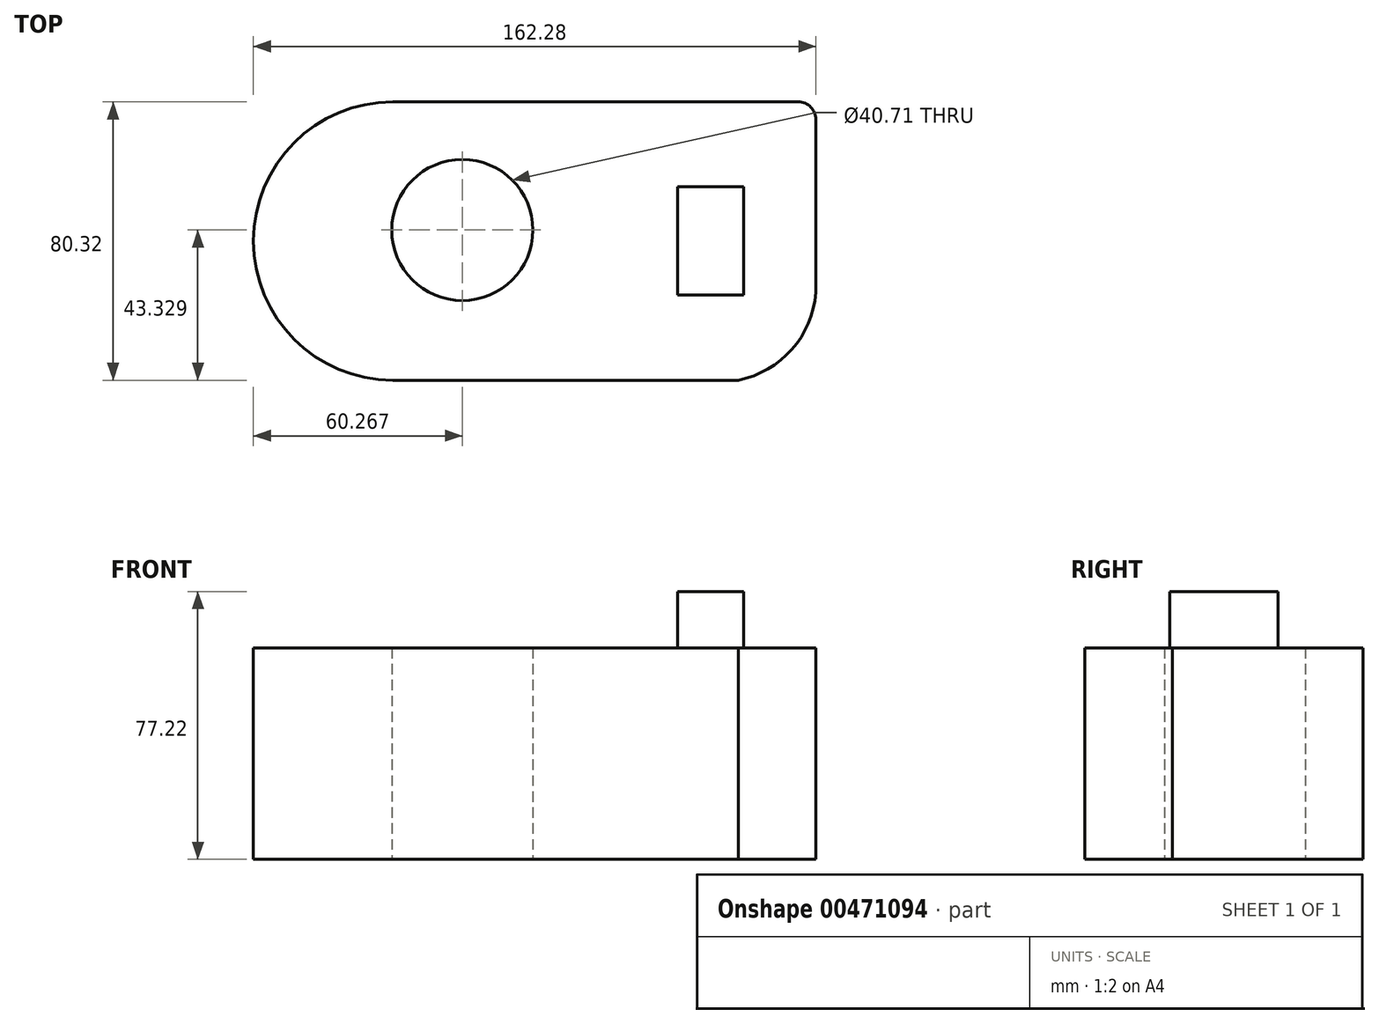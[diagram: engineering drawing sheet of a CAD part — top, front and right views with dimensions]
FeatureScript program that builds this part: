
annotation { "Feature Type Name" : "Feature", "Feature Type Description" : "" }
export const myFeature = defineFeature(function(context is Context, id is Id, definition is map)
    precondition{}
    {
        {
            var Q0;
            Q0=qCreatedBy(makeId("Top.planeOp"),FACE);
            var sketch = newSketch(context, id + "F0", { "sketchPlane" : qUnion([Q0])});
            skLineSegment(sketch, "E0.bottom", {"start": v(61.06, 40.16) * mm, "end": v(-61.06, 40.16) * mm});
            skLineSegment(sketch, "E0.top", {"start": v(38.63, -40.16) * mm, "end": v(-61.06, -40.16) * mm});
            skLineSegment(sketch, "E0.left", {"start": v(61.06, 40.16) * mm, "end": v(61.06, -14.84) * mm});
            skPoint(sketch, "E0.middle", {"position": v(0, 0) * mm});
            skArc(sketch, "E1", {"start": v(-61.06, -40.16) * mm, "mid": v(-101.22, 0) * mm, "end": v(-61.06, 40.16) * mm});
            skArc(sketch, "E2", {"start": v(38.63, -40.16) * mm, "mid": v(54.11, -31.28) * mm, "end": v(61.06, -14.84) * mm});
            skPoint(sketch, "E3.orphan", {"position": v(61.06, -40.16) * mm});
            skCircle(sketch, "E4", {"center": v(-40.95, 3.17) * mm, "radius": 20.35 * mm});
            skPoint(sketch, "E4.second.point", {"position": v(-20.85, 0) * mm});
            skPoint(sketch, "E4.third.point", {"position": v(-61.06, 6.34) * mm});
            skSolve(sketch);
        }
        {
            var Q0;
            Q0=makeQuery(id+"F0.imprint","IMPRINT",FACE,{"disambiguationData":[TD([[makeQuery(id+"F0.imprint","IMPRINT",EDGE,{"derivedFrom":sQuery(id+"F0.wireOp",EDGE,"E0.bottom")}),1.0]])]});
            extrude(context, id + "F1", {"entities" : qUnion([Q0]), "depth" : 60.96 * mm});
        }
        {
            var Q0;
            Q0=makeQuery(id+"F1.opExtrude","SWEPT_EDGE",EDGE,{"disambiguationData":[OSD([sQuery(id+"F0.wireOp",EDGE,"E0.bottom"),sQuery(id+"F0.wireOp",EDGE,"E0.left")])]});
            fillet(context, id + "F2", {"entities" : qUnion([Q0]), "radius" : 5.08 * mm, "tangentPropagation" : true, "allowEdgeOverflow" : false});
        }
        {
            var Q0;
            Q0=makeQuery(id+"F1.opExtrude","CAP_FACE",FACE,{"disambiguationData":[OSD([sQuery(id+"F0.wireOp",EDGE,"E0.bottom"),sQuery(id+"F0.wireOp",EDGE,"E0.top"),sQuery(id+"F0.wireOp",EDGE,"E0.left"),sQuery(id+"F0.wireOp",EDGE,"E1"),sQuery(id+"F0.wireOp",EDGE,"E2"),sQuery(id+"F0.wireOp",EDGE,"E4")])],"isStart":false});
            var sketch = newSketch(context, id + "F3", { "sketchPlane" : qUnion([Q0])});
            skLineSegment(sketch, "E5.bottom", {"start": v(21.18, -15.62) * mm, "end": v(40.24, -15.62) * mm});
            skLineSegment(sketch, "E5.top", {"start": v(21.18, 15.62) * mm, "end": v(40.24, 15.62) * mm});
            skLineSegment(sketch, "E5.left", {"start": v(21.18, -15.62) * mm, "end": v(21.18, 15.62) * mm});
            skLineSegment(sketch, "E5.right", {"start": v(40.24, -15.62) * mm, "end": v(40.24, 15.62) * mm});
            skPoint(sketch, "E5.middle", {"position": v(30.7, 0) * mm});
            skSolve(sketch);
        }
        {
            var Q0;
            Q0 = qSketchRegion(id + "F3", true);
            extrude(context, id + "F4", {"entities" : qUnion([Q0]), "operationType" : NewBodyOperationType.ADD, "depth" : 16.26 * mm});
        }
    });
